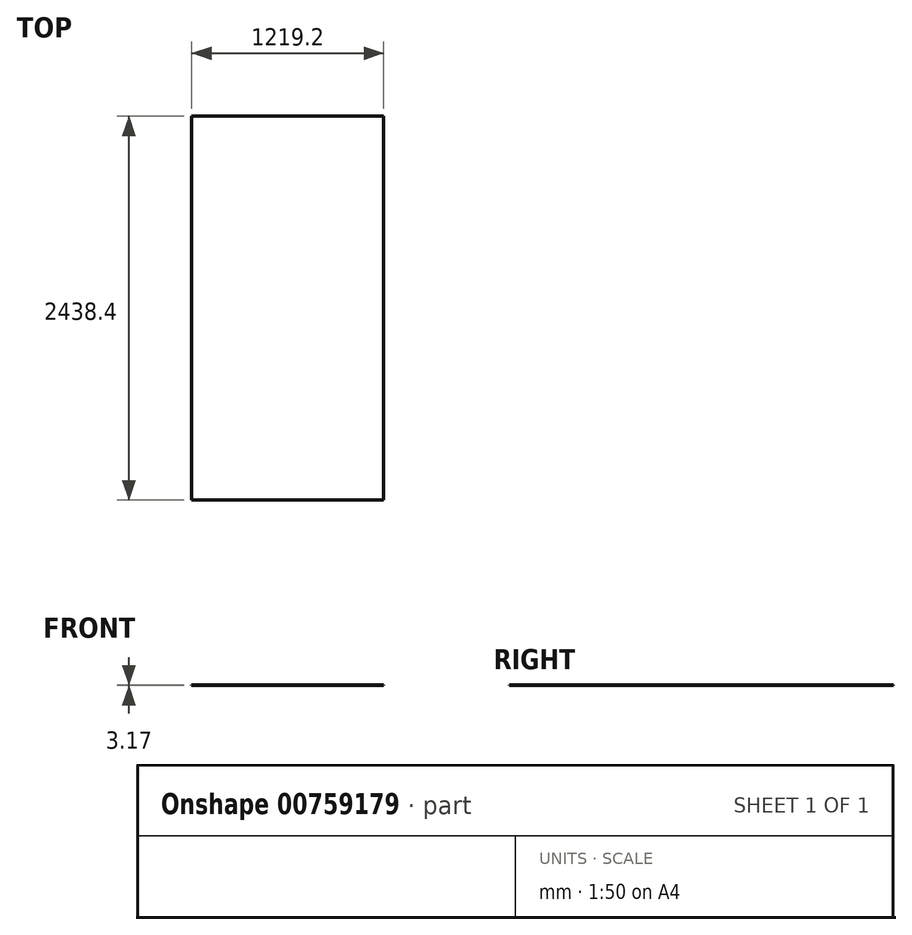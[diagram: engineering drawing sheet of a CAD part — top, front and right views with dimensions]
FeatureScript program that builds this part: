
annotation { "Feature Type Name" : "Feature", "Feature Type Description" : "" }
export const myFeature = defineFeature(function(context is Context, id is Id, definition is map)
    precondition{}
    {
        {
            var Q0;
            Q0=qCreatedBy(makeId("Top.planeOp"),FACE);
            var sketch = newSketch(context, id + "F0", { "sketchPlane" : qUnion([Q0])});
            skLineSegment(sketch, "E0", {"start": v(0, 0) * mm, "end": v(1219.2, 0) * mm});
            skLineSegment(sketch, "E1", {"start": v(1219.2, 0) * mm, "end": v(1219.2, 2438.4) * mm});
            skLineSegment(sketch, "E2", {"start": v(1219.2, 2438.4) * mm, "end": v(0, 2438.4) * mm});
            skLineSegment(sketch, "E3", {"start": v(0, 2438.4) * mm, "end": v(0, 0) * mm});
            skSolve(sketch);
        }
        {
            var Q0;
            Q0=makeQuery(id+"F0.imprint","IMPRINT",FACE,{"disambiguationData":[TD([[makeQuery(id+"F0.imprint","IMPRINT",EDGE,{"derivedFrom":sQuery(id+"F0.wireOp",EDGE,"E0")}),1.0]])]});
            extrude(context, id + "F1", {"entities" : qUnion([Q0]), "depth" : 3.17 * mm, "offsetDistance" : 25.4 * mm});
        }
    });
